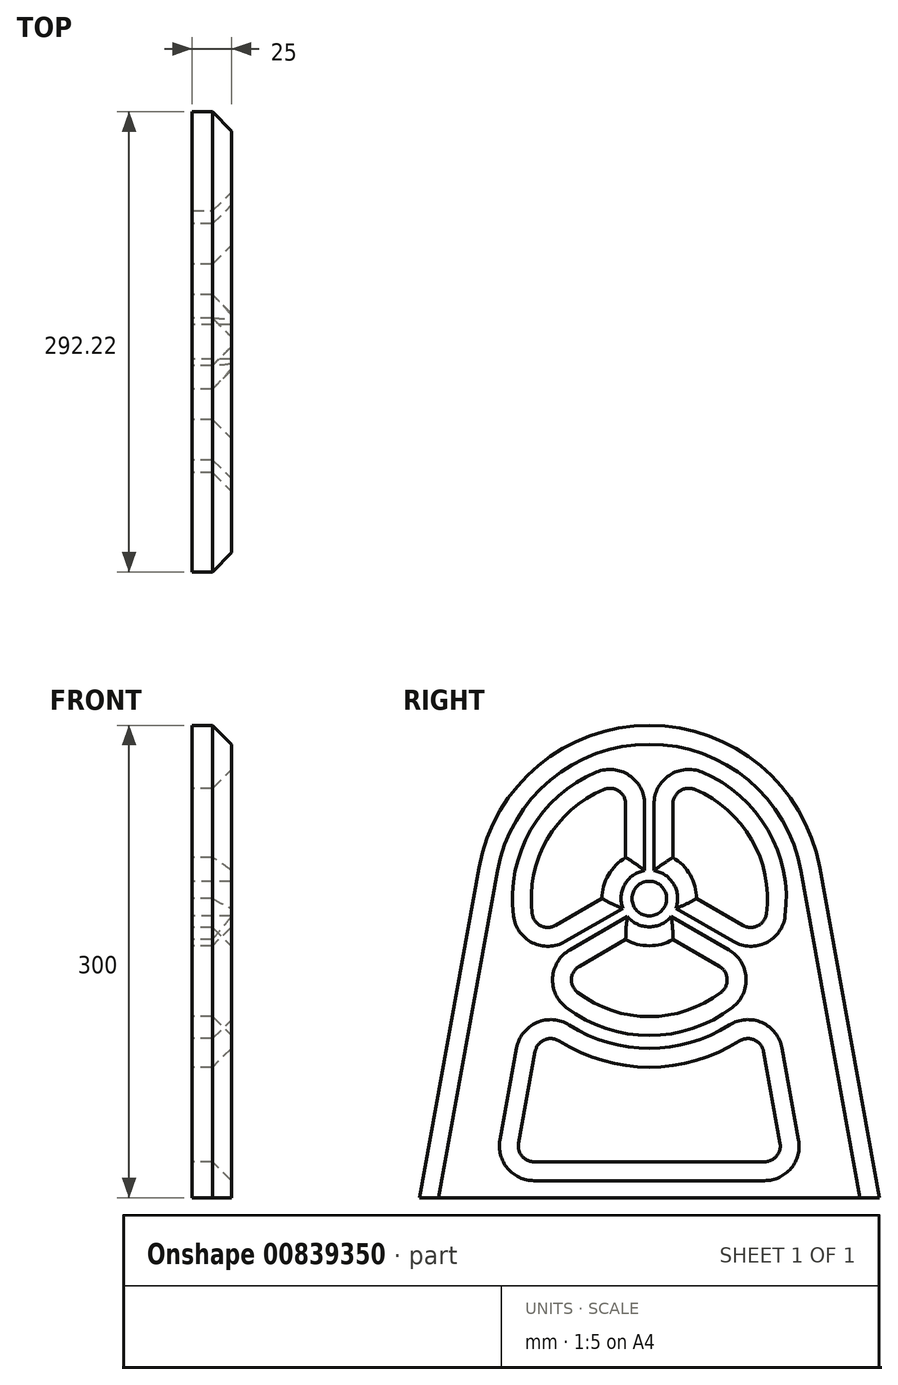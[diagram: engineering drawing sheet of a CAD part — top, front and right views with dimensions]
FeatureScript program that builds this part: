
annotation { "Feature Type Name" : "Feature", "Feature Type Description" : "" }
export const myFeature = defineFeature(function(context is Context, id is Id, definition is map)
    precondition{}
    {
        {
            var Q0;
            Q0=qCreatedBy(makeId("Right.planeOp"),FACE);
            var sketch = newSketch(context, id + "F0", { "sketchPlane" : qUnion([Q0])});
            skLineSegment(sketch, "E0", {"start": v(0, 143.95) * mm, "end": v(0, -207.03) * mm, "construction": true});
            skLineSegment(sketch, "E1", {"start": v(-146.1, -65.56) * mm, "end": v(0, -65.56) * mm});
            skLineSegment(sketch, "E2.MirrorCS", {"start": v(146.1, -65.56) * mm, "end": v(0, -65.56) * mm});
            skCircle(sketch, "E3", {"center": v(0, 124.44) * mm, "radius": 11 * mm});
            skArc(sketch, "E4", {"start": v(108.25, 144) * mm, "mid": v(0, 234.44) * mm, "end": v(-108.25, 144) * mm});
            skLineSegment(sketch, "E5", {"start": v(-108.25, 144) * mm, "end": v(-146.1, -65.56) * mm});
            skLineSegment(sketch, "E6.MirrorCS", {"start": v(108.25, 144) * mm, "end": v(146.1, -65.56) * mm});
            skPoint(sketch, "E7.orphan", {"position": v(-93.45, 225.9) * mm});
            skPoint(sketch, "E8.orphan", {"position": v(93.45, 225.9) * mm});
            skPoint(sketch, "E9.orphan", {"position": v(-154.18, -110.28) * mm});
            skPoint(sketch, "E10.orphan", {"position": v(154.18, -110.28) * mm});
            skArc(sketch, "E11", {"start": v(-69.65, 43.07) * mm, "mid": v(0, 17.33) * mm, "end": v(69.65, 43.07) * mm});
            skLineSegment(sketch, "E12", {"start": v(-69.65, 43.07) * mm, "end": v(-85.16, -42.75) * mm});
            skLineSegment(sketch, "E13", {"start": v(-85.16, -42.75) * mm, "end": v(0, -42.75) * mm});
            skLineSegment(sketch, "E14.MirrorCS", {"start": v(69.65, 43.07) * mm, "end": v(85.16, -42.75) * mm});
            skLineSegment(sketch, "E15.MirrorCS", {"start": v(85.16, -42.75) * mm, "end": v(0, -42.75) * mm});
            skArc(sketch, "E16", {"start": v(-15, 150.42) * mm, "mid": v(-25.98, 139.44) * mm, "end": v(-30, 124.44) * mm});
            skArc(sketch, "E17", {"start": v(-15, 197.92) * mm, "mid": v(-64.95, 161.94) * mm, "end": v(-71.14, 100.69) * mm});
            skLineSegment(sketch, "E18", {"start": v(0, 124.44) * mm, "end": v(0, 199.44) * mm, "construction": true});
            skLineSegment(sketch, "E19", {"start": v(-15, 197.92) * mm, "end": v(-15, 150.42) * mm});
            skLineSegment(sketch, "E20.MirrorCS", {"start": v(15, 197.92) * mm, "end": v(15, 150.42) * mm});
            skLineSegment(sketch, "E21", {"start": v(0, 124.44) * mm, "end": v(-155.34, 34.75) * mm, "construction": true});
            skLineSegment(sketch, "E22.MirrorCS", {"start": v(0, 124.44) * mm, "end": v(155.34, 34.75) * mm, "construction": true});
            skLineSegment(sketch, "E23", {"start": v(-71.14, 100.69) * mm, "end": v(-30, 124.44) * mm});
            skLineSegment(sketch, "E24.MirrorCS", {"start": v(-56.14, 74.7) * mm, "end": v(-15, 98.46) * mm});
            skLineSegment(sketch, "E25.MirrorCS", {"start": v(71.14, 100.69) * mm, "end": v(30, 124.44) * mm});
            skLineSegment(sketch, "E26.MirrorCS", {"start": v(56.14, 74.7) * mm, "end": v(15, 98.46) * mm});
            skArc(sketch, "E27.trimOffspring", {"start": v(71.14, 100.69) * mm, "mid": v(64.95, 161.94) * mm, "end": v(15, 197.92) * mm});
            skArc(sketch, "E28.trimOffspring", {"start": v(30, 124.44) * mm, "mid": v(25.98, 139.44) * mm, "end": v(15, 150.42) * mm});
            skArc(sketch, "E29.trimOffspring", {"start": v(-15, 98.46) * mm, "mid": v(0, 94.44) * mm, "end": v(15, 98.46) * mm});
            skArc(sketch, "E30.trimOffspring", {"start": v(-56.14, 74.7) * mm, "mid": v(0, 49.44) * mm, "end": v(56.14, 74.7) * mm});
            skPoint(sketch, "E31", {"position": v(0, 234.44) * mm});
            skSolve(sketch);
        }
        {
            var Q0;
            Q0=makeQuery(id+"F0.imprint","IMPRINT",FACE,{"disambiguationData":[TD([[makeQuery(id+"F0.imprint","IMPRINT",EDGE,{"derivedFrom":sQuery(id+"F0.wireOp",EDGE,"jEdz9h1V-nbNd-Xhup-E5IR-oE0F7mS6rakX")}),1.0]])]});
            var Q1;
            Q1=makeQuery(id+"F0.imprint","IMPRINT",FACE,{"disambiguationData":[TD([[makeQuery(id+"F0.imprint","IMPRINT",EDGE,{"derivedFrom":sQuery(id+"F0.wireOp",EDGE,"ePafzPjz-uxAR-Yorh-zZCL-BUc0D8Qez3yq")}),1.0]])]});
            var Q2;
            Q2=makeQuery(id+"F0.imprint","IMPRINT",FACE,{"disambiguationData":[TD([[makeQuery(id+"F0.imprint","IMPRINT",EDGE,{"derivedFrom":sQuery(id+"F0.wireOp",EDGE,"E1")}),1.0]])]});
            extrude(context, id + "F1", {"entities" : qUnion([Q0, Q1, Q2]), "endBound" : BoundingType.SYMMETRIC, "depth" : 25 * mm, "offsetDistance" : 25 * mm});
        }
        {
            var Q0;
            Q0=makeQuery(id+"F1.opExtrude","CAP_EDGE",EDGE,{"disambiguationData":[OSD([sQuery(id+"F0.wireOp",EDGE,"E4")])],"isStart":false});
            chamfer(context, id + "F2", {"entities" : qUnion([Q0]), "width" : 12 * mm, "tangentPropagation" : true});
        }
        {
            var Q0;
            Q0=makeQuery(id+"F1.opExtrude","SWEPT_EDGE",EDGE,{"disambiguationData":[OSD([sQuery(id+"F0.wireOp",EDGE,"E11"),sQuery(id+"F0.wireOp",EDGE,"E12")])]});
            var Q1;
            Q1=makeQuery(id+"F1.opExtrude","SWEPT_EDGE",EDGE,{"disambiguationData":[OSD([sQuery(id+"F0.wireOp",EDGE,"E11"),sQuery(id+"F0.wireOp",EDGE,"E14.MirrorCS")])]});
            var Q2;
            Q2=makeQuery(id+"F1.opExtrude","SWEPT_EDGE",EDGE,{"disambiguationData":[OSD([sQuery(id+"F0.wireOp",EDGE,"E12"),sQuery(id+"F0.wireOp",EDGE,"E13")])]});
            var Q3;
            Q3=makeQuery(id+"F1.opExtrude","SWEPT_EDGE",EDGE,{"disambiguationData":[OSD([sQuery(id+"F0.wireOp",EDGE,"E14.MirrorCS"),sQuery(id+"F0.wireOp",EDGE,"E15.MirrorCS")])]});
            var Q4;
            Q4=makeQuery(id+"F1.opExtrude","SWEPT_EDGE",EDGE,{"disambiguationData":[OSD([sQuery(id+"F0.wireOp",EDGE,"E17"),sQuery(id+"F0.wireOp",EDGE,"E19")])]});
            var Q5;
            Q5=makeQuery(id+"F1.opExtrude","SWEPT_EDGE",EDGE,{"disambiguationData":[OSD([sQuery(id+"F0.wireOp",EDGE,"E20.MirrorCS"),sQuery(id+"F0.wireOp",EDGE,"E27.trimOffspring")])]});
            var Q6;
            Q6=makeQuery(id+"F1.opExtrude","SWEPT_EDGE",EDGE,{"disambiguationData":[OSD([sQuery(id+"F0.wireOp",EDGE,"E17"),sQuery(id+"F0.wireOp",EDGE,"E23")])]});
            var Q7;
            Q7=makeQuery(id+"F1.opExtrude","SWEPT_EDGE",EDGE,{"disambiguationData":[OSD([sQuery(id+"F0.wireOp",EDGE,"E24.MirrorCS"),sQuery(id+"F0.wireOp",EDGE,"E30.trimOffspring")])]});
            var Q8;
            Q8=makeQuery(id+"F1.opExtrude","SWEPT_EDGE",EDGE,{"disambiguationData":[OSD([sQuery(id+"F0.wireOp",EDGE,"E26.MirrorCS"),sQuery(id+"F0.wireOp",EDGE,"E30.trimOffspring")])]});
            var Q9;
            Q9=makeQuery(id+"F1.opExtrude","SWEPT_EDGE",EDGE,{"disambiguationData":[OSD([sQuery(id+"F0.wireOp",EDGE,"E25.MirrorCS"),sQuery(id+"F0.wireOp",EDGE,"E27.trimOffspring")])]});
            fillet(context, id + "F3", {"entities" : qUnion([Q0, Q1, Q2, Q3, Q4, Q5, Q6, Q7, Q8, Q9]), "radius" : 10 * mm, "tangentPropagation" : true, "allowEdgeOverflow" : false});
        }
        {
            var Q0;
            Q0=makeQuery(id+"F1.opExtrude","CAP_EDGE",EDGE,{"disambiguationData":[OSD([sQuery(id+"F0.wireOp",EDGE,"E11")])],"isStart":false});
            var Q1;
            Q1=makeQuery(id+"F1.opExtrude","CAP_EDGE",EDGE,{"disambiguationData":[OSD([sQuery(id+"F0.wireOp",EDGE,"E17")])],"isStart":false});
            var Q2;
            Q2=makeQuery(id+"F1.opExtrude","CAP_EDGE",EDGE,{"disambiguationData":[OSD([sQuery(id+"F0.wireOp",EDGE,"E27.trimOffspring")])],"isStart":false});
            var Q3;
            Q3=makeQuery(id+"F1.opExtrude","CAP_EDGE",EDGE,{"disambiguationData":[OSD([sQuery(id+"F0.wireOp",EDGE,"E30.trimOffspring")])],"isStart":false});
            var Q4;
            Q4=makeQuery(id+"F1.opExtrude","CAP_EDGE",EDGE,{"disambiguationData":[OSD([sQuery(id+"F0.wireOp",EDGE,"E16")])],"isStart":false});
            var Q5;
            Q5=makeQuery(id+"F1.opExtrude","CAP_EDGE",EDGE,{"disambiguationData":[OSD([sQuery(id+"F0.wireOp",EDGE,"E29.trimOffspring")])],"isStart":false});
            var Q6;
            Q6=makeQuery(id+"F1.opExtrude","CAP_EDGE",EDGE,{"disambiguationData":[OSD([sQuery(id+"F0.wireOp",EDGE,"E28.trimOffspring")])],"isStart":false});
            chamfer(context, id + "F4", {"entities" : qUnion([Q0, Q1, Q2, Q3, Q4, Q5, Q6]), "width" : 12 * mm, "tangentPropagation" : true});
        }
    });
